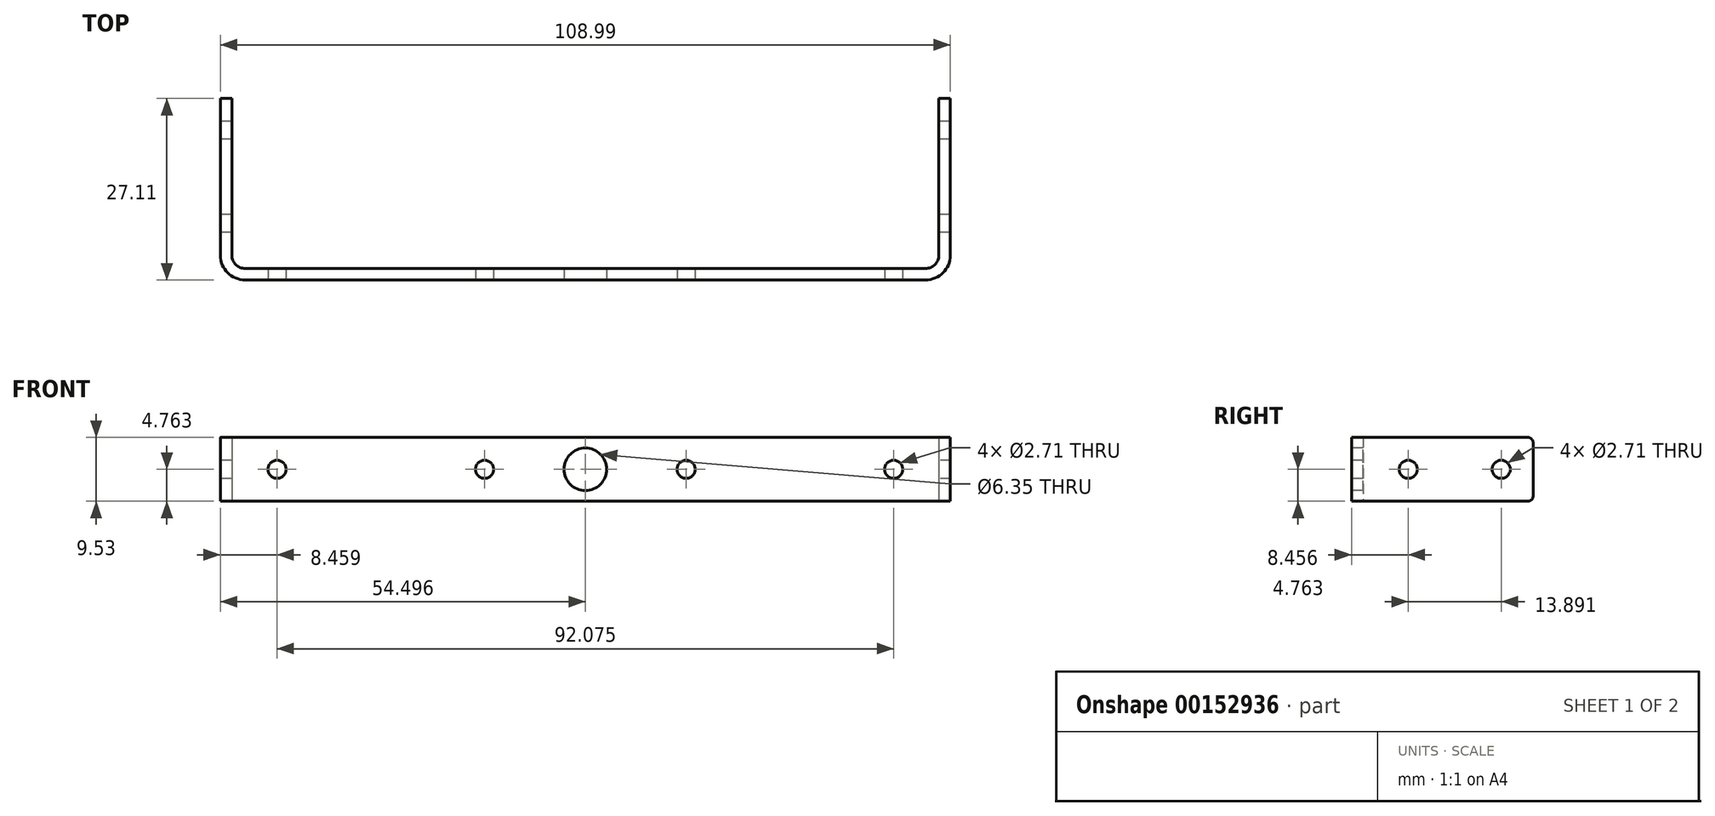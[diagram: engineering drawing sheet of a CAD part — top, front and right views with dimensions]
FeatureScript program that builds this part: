
annotation { "Feature Type Name" : "Feature", "Feature Type Description" : "" }
export const myFeature = defineFeature(function(context is Context, id is Id, definition is map)
    precondition{}
    {
        {
            var Q0;
            Q0=qCreatedBy(makeId("Top.planeOp"),FACE);
            var sketch = newSketch(context, id + "F0", { "sketchPlane" : qUnion([Q0])});
            skLineSegment(sketch, "E0.bottom", {"start": v(0, 0) * mm, "end": v(-105.57, 0) * mm});
            skLineSegment(sketch, "E0.top", {"start": v(1.7, -1.7) * mm, "end": v(-107.28, -1.7) * mm});
            skLineSegment(sketch, "E1.top", {"start": v(-105.57, 25.4) * mm, "end": v(-107.28, 25.4) * mm});
            skLineSegment(sketch, "E1.left", {"start": v(-105.57, 0) * mm, "end": v(-105.57, 25.4) * mm});
            skLineSegment(sketch, "E1.right", {"start": v(-107.28, -1.7) * mm, "end": v(-107.28, 25.4) * mm});
            skLineSegment(sketch, "E2.top", {"start": v(0, 25.4) * mm, "end": v(1.7, 25.4) * mm});
            skLineSegment(sketch, "E2.left", {"start": v(0, 0) * mm, "end": v(0, 25.4) * mm});
            skLineSegment(sketch, "E2.right", {"start": v(1.7, -1.7) * mm, "end": v(1.7, 25.4) * mm});
            skLineSegment(sketch, "E3", {"start": v(-52.78, 0) * mm, "end": v(-52.78, -1.7) * mm, "construction": true});
            skSolve(sketch);
        }
        {
            var Q0;
            Q0=qSketchRegion(id+"F0",true);
            extrude(context, id + "F1", {"entities" : qUnion([Q0]), "depth" : 9.52 * mm});
        }
        {
            var Q0;
            Q0=makeQuery(id+"FcdIcV9w6YY9zah_1.opExtrude","CAP_EDGE",EDGE,{"disambiguationData":[OSD([sQuery(id+"FU7sgaIbCbRhSfr_1.wireOp",EDGE,"F29Sxc5V-O2cl-wjtz-gx5o-reTTBG7m1pNU.top")])],"isStart":true});
            var Q1;
            Q1=makeQuery(id+"FcdIcV9w6YY9zah_1.opExtrude","CAP_EDGE",EDGE,{"disambiguationData":[OSD([sQuery(id+"FU7sgaIbCbRhSfr_1.wireOp",EDGE,"yv2bQU74-Eht6-uYuo-WBF2-3C4kyuaz0slr.top")])],"isStart":true});
            var Q2;
            Q2=makeQuery(id+"F1.opExtrude","SWEPT_EDGE",EDGE,{"disambiguationData":[OSD([sQuery(id+"F0.wireOp",EDGE,"E0.bottom"),sQuery(id+"F0.wireOp",EDGE,"E2.left")])]});
            var Q3;
            Q3=makeQuery(id+"F1.opExtrude","SWEPT_EDGE",EDGE,{"disambiguationData":[OSD([sQuery(id+"F0.wireOp",EDGE,"E0.bottom"),sQuery(id+"F0.wireOp",EDGE,"E1.left")])]});
            fillet(context, id + "F2", {"entities" : qUnion([Q0, Q1, Q2, Q3]), "radius" : 1.98 * mm, "tangentPropagation" : true, "allowEdgeOverflow" : false});
        }
        {
            var Q0;
            Q0=makeQuery(id+"FkwQQH4eT4IjhdK_1.opExtrude","CAP_EDGE",EDGE,{"disambiguationData":[OSD([sQuery(id+"FvDFSbhwMPyTNrQ_1.wireOp",EDGE,"223FG13h-YrEq-unoX-9EOi-DwKLLmwbrteD.top")])],"isStart":false});
            var Q1;
            Q1=makeQuery(id+"F1.opExtrude","SWEPT_EDGE",EDGE,{"disambiguationData":[OSD([sQuery(id+"F0.wireOp",EDGE,"E0.top"),sQuery(id+"F0.wireOp",EDGE,"E2.right")])]});
            var Q2;
            Q2=makeQuery(id+"F1.opExtrude","SWEPT_EDGE",EDGE,{"disambiguationData":[OSD([sQuery(id+"F0.wireOp",EDGE,"E0.top"),sQuery(id+"F0.wireOp",EDGE,"E1.right")])]});
            var Q3;
            Q3=makeQuery(id+"F2kHonbXZaQoFrR_1.opExtrude","CAP_EDGE",EDGE,{"disambiguationData":[OSD([sQuery(id+"FsAbJG8AZOSwdHE_1.wireOp",EDGE,"WRaIy3id-o2EU-qHqw-IwdC-eHQZRSiK4KpF.bottom")])],"isStart":false});
            fillet(context, id + "F3", {"entities" : qUnion([Q0, Q1, Q2, Q3]), "radius" : 3.7 * mm, "tangentPropagation" : true, "allowEdgeOverflow" : false});
        }
        {
            var Q0;
            Q0=makeQuery(id+"F1.opExtrude","SWEPT_FACE",FACE,{"disambiguationData":[OSD([sQuery(id+"F0.wireOp",EDGE,"E1.right")])]});
            var sketch = newSketch(context, id + "F4", { "sketchPlane" : qUnion([Q0])});
            skLineSegment(sketch, "E4", {"start": v(-25.4, 4.76) * mm, "end": v(-20.64, 4.76) * mm, "construction": true});
            skLineSegment(sketch, "E5", {"start": v(-20.64, 4.76) * mm, "end": v(-6.75, 4.76) * mm, "construction": true});
            skLineSegment(sketch, "E6", {"start": v(-6.75, 4.76) * mm, "end": v(-1.98, 4.76) * mm, "construction": true});
            skLineSegment(sketch, "E7", {"start": v(-20.64, 4.76) * mm, "end": v(-20.64, 0) * mm, "construction": true});
            skCircle(sketch, "E8", {"center": v(-20.64, 4.76) * mm, "radius": 1.35 * mm});
            skCircle(sketch, "E9", {"center": v(-6.75, 4.76) * mm, "radius": 1.35 * mm});
            skSolve(sketch);
        }
        {
            var Q0;
            Q0=qSketchRegion(id+"F4",true);
            var Q1;
            Q1=makeQuery(id+"F1.opExtrude","SWEPT_FACE",FACE,{"disambiguationData":[OSD([sQuery(id+"F0.wireOp",EDGE,"E2.right")])]});
            extrude(context, id + "F5", {"entities" : qUnion([Q0]), "operationType" : NewBodyOperationType.REMOVE, "endBound" : BoundingType.UP_TO_SURFACE, "oppositeDirection" : true, "endBoundEntityFace" : qUnion([Q1]), "depth" : 25.4 * mm});
        }
        {
            var Q0;
            Q0=makeQuery(id+"F1.opExtrude","SWEPT_FACE",FACE,{"disambiguationData":[OSD([sQuery(id+"F0.wireOp",EDGE,"E0.top")])]});
            var sketch = newSketch(context, id + "F6", { "sketchPlane" : qUnion([Q0])});
            skCircle(sketch, "E10", {"center": v(-98.82, 4.76) * mm, "radius": 1.35 * mm});
            skCircle(sketch, "E11", {"center": v(-6.75, 4.76) * mm, "radius": 1.35 * mm});
            skLineSegment(sketch, "E12", {"start": v(-98.82, 4.76) * mm, "end": v(-103.58, 4.76) * mm, "construction": true});
            skLineSegment(sketch, "E13", {"start": v(-52.78, 4.76) * mm, "end": v(-52.78, 9.53) * mm, "construction": true});
            skLineSegment(sketch, "E14", {"start": v(-6.75, 4.76) * mm, "end": v(-1.98, 4.76) * mm, "construction": true});
            skLineSegment(sketch, "E15", {"start": v(-98.82, 4.76) * mm, "end": v(-67.84, 4.76) * mm, "construction": true});
            skLineSegment(sketch, "E16", {"start": v(-67.84, 4.76) * mm, "end": v(-37.73, 4.76) * mm, "construction": true});
            skLineSegment(sketch, "E17", {"start": v(-37.73, 4.76) * mm, "end": v(-6.75, 4.76) * mm, "construction": true});
            skCircle(sketch, "E18", {"center": v(-67.84, 4.76) * mm, "radius": 1.35 * mm});
            skCircle(sketch, "E19", {"center": v(-37.73, 4.76) * mm, "radius": 1.35 * mm});
            skCircle(sketch, "E20", {"center": v(-52.78, 4.76) * mm, "radius": 3.18 * mm});
            skSolve(sketch);
        }
        {
            var Q0;
            Q0=qSketchRegion(id+"F6",true);
            var Q1;
            Q1=makeQuery(id+"F1.opExtrude","SWEPT_FACE",FACE,{"disambiguationData":[OSD([sQuery(id+"F0.wireOp",EDGE,"E0.bottom")])]});
            extrude(context, id + "F7", {"entities" : qUnion([Q0]), "operationType" : NewBodyOperationType.REMOVE, "endBound" : BoundingType.UP_TO_SURFACE, "oppositeDirection" : true, "endBoundEntityFace" : qUnion([Q1]), "depth" : 25.4 * mm});
        }
        {
            var Q0;
            Q0=makeQuery(id+"F1.opExtrude","CAP_EDGE",EDGE,{"disambiguationData":[OSD([sQuery(id+"F0.wireOp",EDGE,"E1.top")])],"isStart":false});
            var Q1;
            Q1=makeQuery(id+"F1.opExtrude","CAP_EDGE",EDGE,{"disambiguationData":[OSD([sQuery(id+"F0.wireOp",EDGE,"E1.top")])],"isStart":true});
            var Q2;
            Q2=makeQuery(id+"F1.opExtrude","CAP_EDGE",EDGE,{"disambiguationData":[OSD([sQuery(id+"F0.wireOp",EDGE,"E2.top")])],"isStart":false});
            var Q3;
            Q3=makeQuery(id+"F1.opExtrude","CAP_EDGE",EDGE,{"disambiguationData":[OSD([sQuery(id+"F0.wireOp",EDGE,"E2.top")])],"isStart":true});
            fillet(context, id + "F8", {"entities" : qUnion([Q0, Q1, Q2, Q3]), "radius" : 0.76 * mm, "tangentPropagation" : true, "allowEdgeOverflow" : false});
        }
    });
